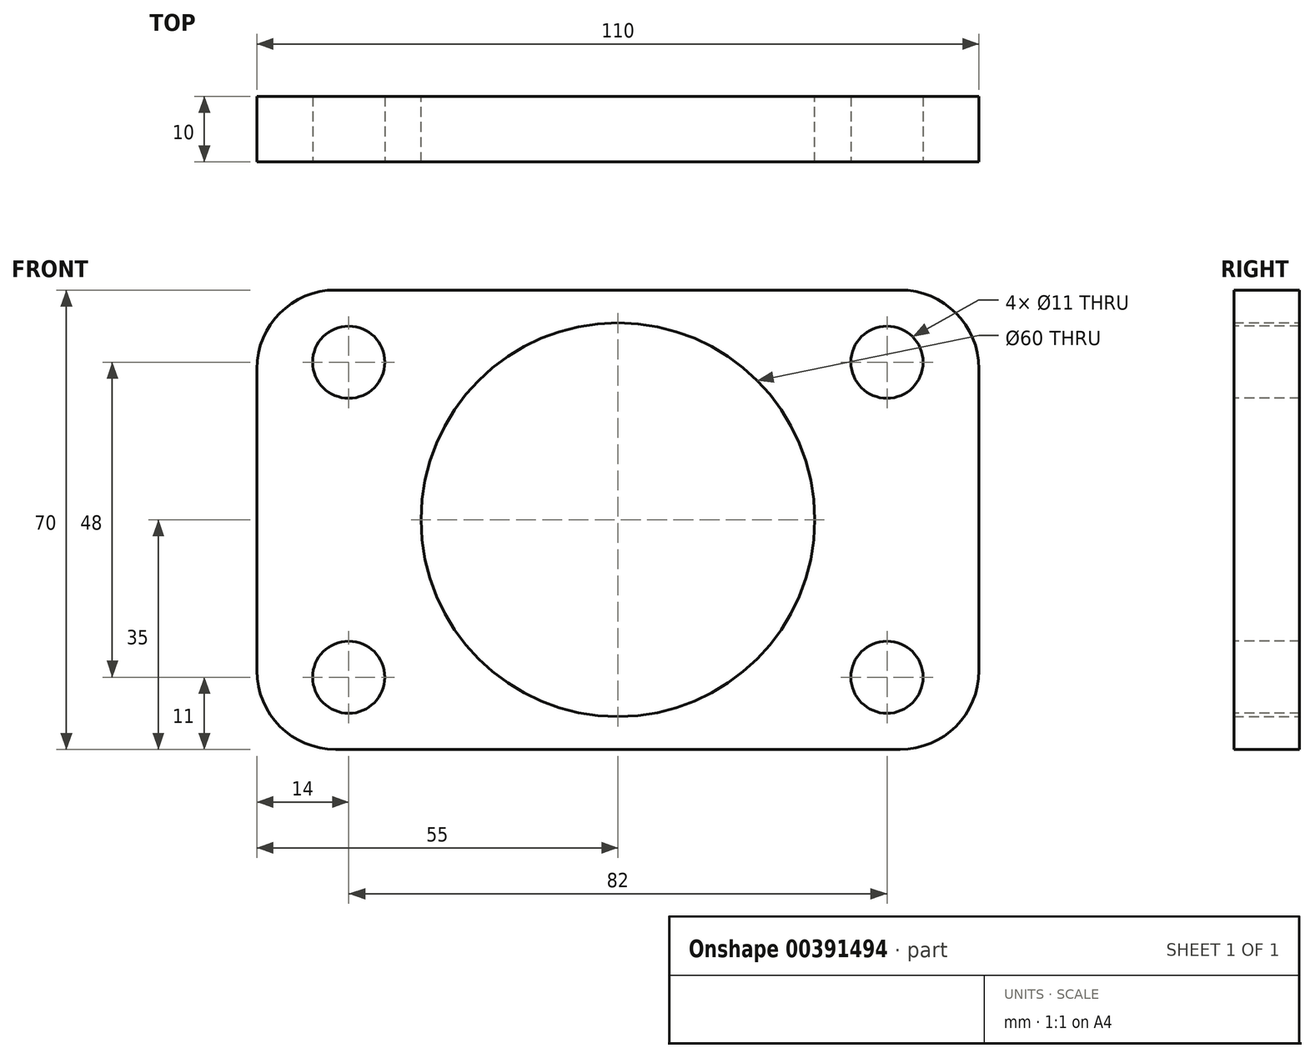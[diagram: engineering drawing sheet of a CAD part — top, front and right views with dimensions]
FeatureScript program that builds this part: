
annotation { "Feature Type Name" : "Feature", "Feature Type Description" : "" }
export const myFeature = defineFeature(function(context is Context, id is Id, definition is map)
    precondition{}
    {
        {
            var Q0;
            Q0=qCreatedBy(makeId("Front.planeOp"),FACE);
            var sketch = newSketch(context, id + "F0", { "sketchPlane" : qUnion([Q0])});
            skCircle(sketch, "E0", {"center": v(0, 0) * mm, "radius": 30 * mm});
            skLineSegment(sketch, "E1.bottom", {"start": v(43, 35) * mm, "end": v(-43, 35) * mm});
            skLineSegment(sketch, "E1.top", {"start": v(43, -35) * mm, "end": v(-43, -35) * mm});
            skLineSegment(sketch, "E1.left", {"start": v(55, 23) * mm, "end": v(55, -23) * mm});
            skLineSegment(sketch, "E1.right", {"start": v(-55, 23) * mm, "end": v(-55, -23) * mm});
            skLineSegment(sketch, "E2.bottom", {"start": v(41, -24) * mm, "end": v(-41, -24) * mm, "construction": true});
            skLineSegment(sketch, "E2.top", {"start": v(41, 24) * mm, "end": v(-41, 24) * mm, "construction": true});
            skLineSegment(sketch, "E2.left", {"start": v(41, -24) * mm, "end": v(41, 24) * mm, "construction": true});
            skLineSegment(sketch, "E2.right", {"start": v(-41, -24) * mm, "end": v(-41, 24) * mm, "construction": true});
            skPoint(sketch, "E3.visualSharp", {"position": v(-55, 35) * mm});
            skArc(sketch, "E3.filletArc", {"start": v(-43, 35) * mm, "mid": v(-51.49, 31.49) * mm, "end": v(-55, 23) * mm});
            skPoint(sketch, "E4.visualSharp", {"position": v(55, 35) * mm});
            skArc(sketch, "E4.filletArc", {"start": v(55, 23) * mm, "mid": v(51.49, 31.49) * mm, "end": v(43, 35) * mm});
            skPoint(sketch, "E5.visualSharp", {"position": v(55, -35) * mm});
            skArc(sketch, "E5.filletArc", {"start": v(43, -35) * mm, "mid": v(51.49, -31.49) * mm, "end": v(55, -23) * mm});
            skPoint(sketch, "E6.visualSharp", {"position": v(-55, -35) * mm});
            skArc(sketch, "E6.filletArc", {"start": v(-55, -23) * mm, "mid": v(-51.49, -31.49) * mm, "end": v(-43, -35) * mm});
            skSolve(sketch);
        }
        {
            var Q0;
            Q0=makeQuery(id+"F0.imprint","IMPRINT",FACE,{"disambiguationData":[TD([[makeQuery(id+"F0.imprint","IMPRINT",EDGE,{"derivedFrom":sQuery(id+"F0.wireOp",EDGE,"E0")}),-1.0]])]});
            extrude(context, id + "F1", {"entities" : qUnion([Q0]), "depth" : 10 * mm});
        }
        {
            var Q0;
            Q0=sQuery(id+"F0.wireOp",VERTEX,"E2.right.end");
            var Q1;
            Q1=sQuery(id+"F0.wireOp",VERTEX,"E2.left.end");
            var Q2;
            Q2=sQuery(id+"F0.wireOp",VERTEX,"E2.left.start");
            var Q3;
            Q3=sQuery(id+"F0.wireOp",VERTEX,"E2.right.start");
            var Q4;
            Q4=makeQuery(id+"F1.opExtrude","SWEPT_BODY",BODY,{"disambiguationData":[OSD([sQuery(id+"F0.wireOp",EDGE,"E0"),sQuery(id+"F0.wireOp",EDGE,"E1.bottom"),sQuery(id+"F0.wireOp",EDGE,"E1.top"),sQuery(id+"F0.wireOp",EDGE,"E1.left"),sQuery(id+"F0.wireOp",EDGE,"E1.right")])]});
            hole(context, id + "F2", {"style" : HoleStyle.SIMPLE, "endStyle" : HoleEndStyle.THROUGH, "oppositeDirection" : true, "holeDiameter" : 11 * mm, "isTappedThrough" : true, "tappedDepth" : 12 * mm, "tapClearance" : 3, "locations" : qUnion([Q0, Q1, Q2, Q3]), "scope" : qUnion([Q4]), "startStyle" : HoleStartStyle.SKETCH});
        }
    });
